# Revit family: Faucet-Lavatory-KOHLER-Aleo-K-72278IN_1
name_source: partatom
category: Plumbing Fixtures
revit_build: Autodesk Revit 2017 (Build: 20160225_1515(x64)
units: mm (PartAtom-declared; Revit-internal decimal feet)

## family parameters
Cut with Voids When Loaded = No
Host = Face
OmniClass Number = 23.31.11.00
OmniClass Title = Faucets
Part Type = Normal
Room Calculation Point = No
Round Connector Dimension = Use Diameter
Shared = No

## types (2) — shared parameters
ADA Compliant = No
Assembly Code = D2010
CW Connection = Yes
Cold Water Inlet = Cold Water Inlet
Date Modified = 10/07/2020
Default Elevation = 36"
Finish = Kohler-Metal-CP-Polished_Chrome
Flow Rate = 3 GPM
HW Connection = Yes
Handle Clearance = 3 5/8"
Height = 11 5/16"
Hot Water Inlet = Hot Water Inlet
Length = 6 1/16"
Manufacturer = KOHLER Co.
Master Format 2014 = 22 41 39
Master Format 2014 Name = Residential Faucets, Supplies, and Trim
Material = Premium Metal Construction
Pressure = 60.00 psi
Product Name = Aleo
Spout Reach = 6 1/16"
URL = https://www.kohler.co.in
Vent Connection = No
Waste Connection = No
Waste Water Outlet = Waste Water Outlet
WaterSense Certified = No
Width = 2"

## per-type parameters (varying)
| type | Description | Drain | Drain Included | Model | Product Documentation Link | Product Page URL | Type |
| With Drain, CP-Polished Chrome | Single-control lavatory faucet with swivel spout, with drain | Yes | Yes | K-72278IN-4-CP |  |  | 1 |
| Without Drain, CP-Polished Chrome | Single-control lavatory faucet with swivel spout, without drain | No | No | K-72278IN-4ND-CP | http://resources.kohler.com | https://www.kohler.co.in | 2 |

## geometry (parser evidence)
native form markers: Sweep x6
no freeform markers — native parametric forms only
